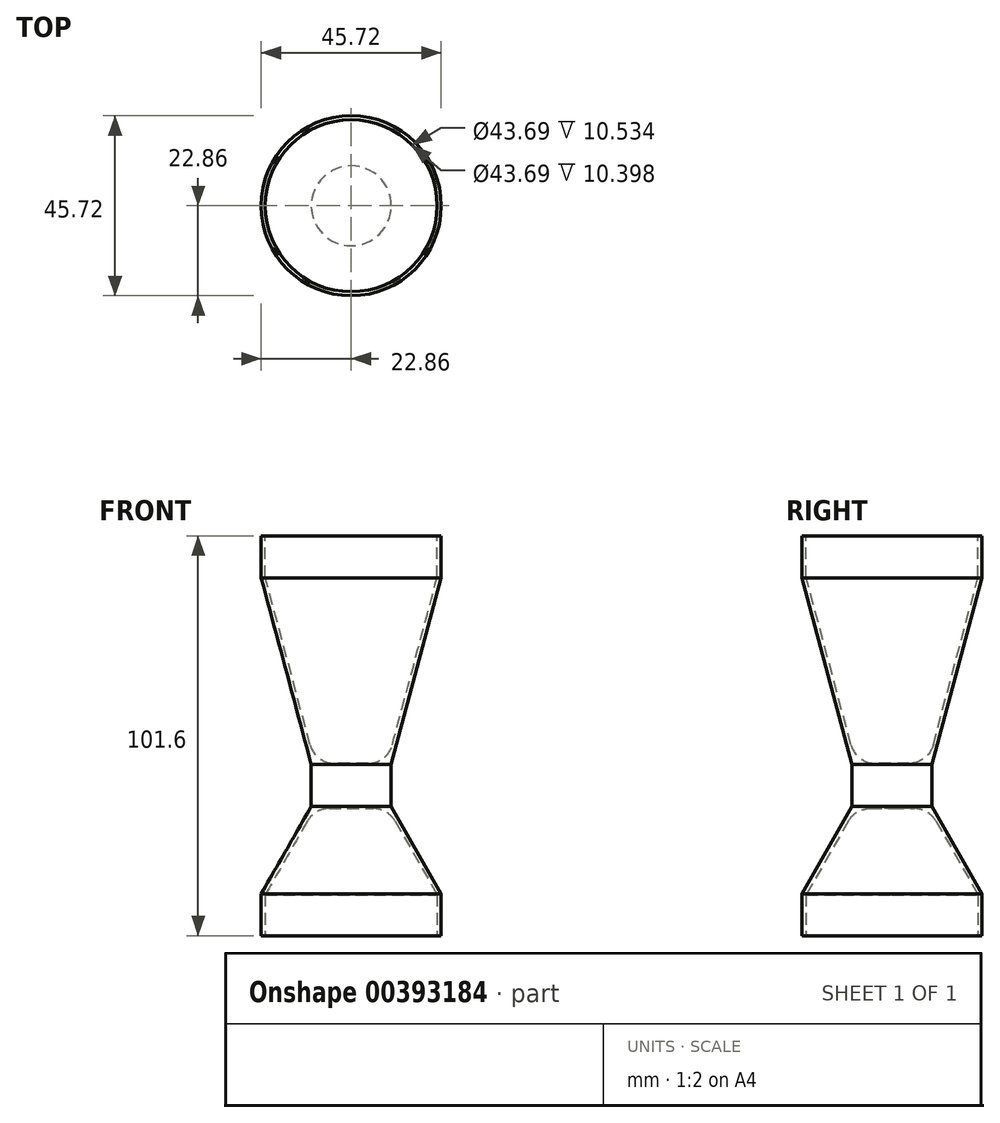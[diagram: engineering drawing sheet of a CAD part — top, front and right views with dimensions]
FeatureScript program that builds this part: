
annotation { "Feature Type Name" : "Feature", "Feature Type Description" : "" }
export const myFeature = defineFeature(function(context is Context, id is Id, definition is map)
    precondition{}
    {
        {
            var Q0;
            Q0=qCreatedBy(makeId("Front.planeOp"),FACE);
            var sketch = newSketch(context, id + "F0", { "sketchPlane" : qUnion([Q0])});
            skLineSegment(sketch, "E0", {"start": v(22.86, 50.45) * mm, "end": v(22.86, 39.78) * mm});
            skLineSegment(sketch, "E1", {"start": v(22.86, 39.78) * mm, "end": v(10.16, -7.62) * mm});
            skLineSegment(sketch, "E2", {"start": v(10.16, -7.62) * mm, "end": v(10.16, -18.29) * mm});
            skLineSegment(sketch, "E3", {"start": v(10.16, -18.29) * mm, "end": v(22.86, -40.49) * mm});
            skLineSegment(sketch, "E4", {"start": v(22.86, -40.49) * mm, "end": v(22.86, -51.15) * mm});
            skLineSegment(sketch, "E5", {"start": v(22.86, -51.15) * mm, "end": v(0, -51.15) * mm});
            skLineSegment(sketch, "E6", {"start": v(0, -51.15) * mm, "end": v(0, 50.45) * mm});
            skLineSegment(sketch, "E7", {"start": v(0, 50.45) * mm, "end": v(22.86, 50.45) * mm});
            skSolve(sketch);
        }
        {
            var Q0;
            Q0=makeQuery(id+"F0.imprint","IMPRINT",FACE,{"disambiguationData":[TD([[makeQuery(id+"F0.imprint","IMPRINT",EDGE,{"derivedFrom":sQuery(id+"F0.wireOp",EDGE,"E0")}),-1.0]])]});
            var Q1;
            Q1=sQuery(id+"F0.wireOp",EDGE,"E6");
            revolve(context, id + "F1", {"entities" : qUnion([Q0]), "axis" : qUnion([Q1]), "revolveType" : RevolveType.FULL});
        }
        {
            var Q0;
            Q0=qCreatedBy(makeId("Front.planeOp"),FACE);
            var sketch = newSketch(context, id + "F2", { "sketchPlane" : qUnion([Q0])});
            skLineSegment(sketch, "E8.0", {"start": v(21.84, 39.91) * mm, "end": v(10.44, -2.65) * mm});
            skLineSegment(sketch, "E9.0", {"start": v(21.84, 50.45) * mm, "end": v(21.84, 39.91) * mm});
            skLineSegment(sketch, "E10", {"start": v(4.3, -7.36) * mm, "end": v(0, -7.36) * mm});
            skLineSegment(sketch, "E11", {"start": v(0, -7.36) * mm, "end": v(0, 50.45) * mm});
            skLineSegment(sketch, "E12", {"start": v(0, 50.45) * mm, "end": v(21.84, 50.45) * mm});
            skPoint(sketch, "E13.visualSharp", {"position": v(9.18, -7.36) * mm});
            skArc(sketch, "E13.filletArc", {"start": v(4.3, -7.36) * mm, "mid": v(8.17, -6.04) * mm, "end": v(10.44, -2.65) * mm});
            skSolve(sketch);
        }
        {
            var Q0;
            Q0 = qSketchRegion(id + "F2", true);
            var Q1;
            Q1=sQuery(id+"F2.wireOp",EDGE,"E11");
            revolve(context, id + "F3", {"operationType" : NewBodyOperationType.REMOVE, "entities" : qUnion([Q0]), "axis" : qUnion([Q1]), "revolveType" : RevolveType.FULL, "oppositeDirection" : true});
        }
        {
            var Q0;
            Q0=qCreatedBy(makeId("Front.planeOp"),FACE);
            var sketch = newSketch(context, id + "F4", { "sketchPlane" : qUnion([Q0])});
            skLineSegment(sketch, "E14.0", {"start": v(11.13, -22.04) * mm, "end": v(21.84, -40.76) * mm});
            skLineSegment(sketch, "E15.0", {"start": v(21.84, -40.76) * mm, "end": v(21.84, -51.15) * mm});
            skLineSegment(sketch, "E16", {"start": v(5.62, -18.84) * mm, "end": v(0, -18.84) * mm});
            skLineSegment(sketch, "E17", {"start": v(0, -18.84) * mm, "end": v(0, -51.15) * mm});
            skLineSegment(sketch, "E18", {"start": v(0, -51.15) * mm, "end": v(21.84, -51.15) * mm});
            skPoint(sketch, "E19.visualSharp", {"position": v(9.3, -18.84) * mm});
            skArc(sketch, "E19.filletArc", {"start": v(11.13, -22.04) * mm, "mid": v(8.8, -19.7) * mm, "end": v(5.62, -18.84) * mm});
            skSolve(sketch);
        }
        {
            var Q0;
            Q0 = qSketchRegion(id + "F4", true);
            var Q1;
            Q1=sQuery(id+"F4.wireOp",EDGE,"E17");
            revolve(context, id + "F5", {"operationType" : NewBodyOperationType.REMOVE, "entities" : qUnion([Q0]), "axis" : qUnion([Q1]), "revolveType" : RevolveType.FULL, "oppositeDirection" : true});
        }
    });
